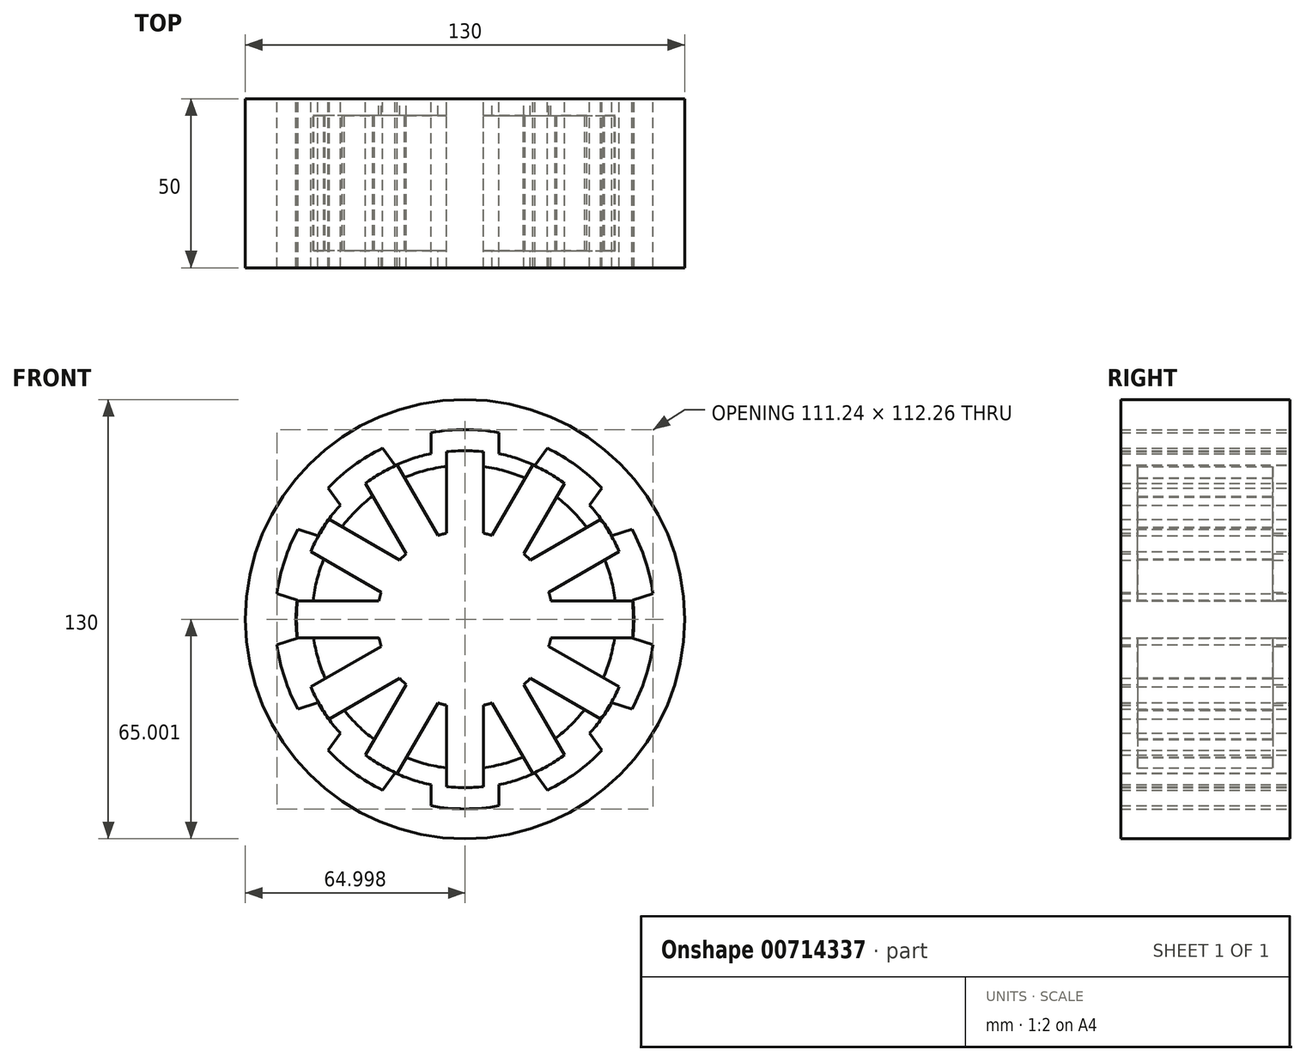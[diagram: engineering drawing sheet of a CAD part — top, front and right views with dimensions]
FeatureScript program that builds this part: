
annotation { "Feature Type Name" : "Feature", "Feature Type Description" : "" }
export const myFeature = defineFeature(function(context is Context, id is Id, definition is map)
    precondition{}
    {
        {
            var Q0;
            Q0=qCreatedBy(makeId("Front.planeOp"),FACE);
            var sketch = newSketch(context, id + "F0", { "sketchPlane" : qUnion([Q0])});
            skLineSegment(sketch, "E0.left", {"start": v(-130.96, 40.1) * mm, "end": v(-130.96, 33.86) * mm});
            skLineSegment(sketch, "E0.right", {"start": v(-110.96, 40.1) * mm, "end": v(-110.96, 33.86) * mm});
            skLineSegment(sketch, "E1.1.0", {"start": v(-145.34, 35.43) * mm, "end": v(-141.67, 30.38) * mm});
            skLineSegment(sketch, "E1.1.3", {"start": v(-161.52, 23.68) * mm, "end": v(-157.85, 18.63) * mm});
            skLineSegment(sketch, "E1.2.0", {"start": v(-170.4, 11.45) * mm, "end": v(-164.46, 9.52) * mm});
            skLineSegment(sketch, "E1.2.3", {"start": v(-176.58, -7.57) * mm, "end": v(-170.64, -9.5) * mm});
            skLineSegment(sketch, "E1.3.0", {"start": v(-176.58, -22.69) * mm, "end": v(-170.64, -20.76) * mm});
            skLineSegment(sketch, "E1.3.3", {"start": v(-170.4, -41.7) * mm, "end": v(-164.46, -39.78) * mm});
            skLineSegment(sketch, "E1.4.0", {"start": v(-161.52, -53.94) * mm, "end": v(-157.85, -48.89) * mm});
            skLineSegment(sketch, "E1.4.3", {"start": v(-145.34, -65.7) * mm, "end": v(-141.67, -60.64) * mm});
            skLineSegment(sketch, "E1.5.0", {"start": v(-130.96, -70.36) * mm, "end": v(-130.96, -64.12) * mm});
            skLineSegment(sketch, "E1.5.3", {"start": v(-110.96, -70.36) * mm, "end": v(-110.96, -64.12) * mm});
            skLineSegment(sketch, "E1.6.0", {"start": v(-96.59, -65.7) * mm, "end": v(-100.26, -60.64) * mm});
            skLineSegment(sketch, "E1.6.3", {"start": v(-80.4, -53.94) * mm, "end": v(-84.08, -48.89) * mm});
            skLineSegment(sketch, "E1.7.0", {"start": v(-71.52, -41.7) * mm, "end": v(-77.46, -39.78) * mm});
            skLineSegment(sketch, "E1.7.3", {"start": v(-65.34, -22.69) * mm, "end": v(-71.28, -20.76) * mm});
            skLineSegment(sketch, "E1.8.0", {"start": v(-65.34, -7.57) * mm, "end": v(-71.28, -9.5) * mm});
            skLineSegment(sketch, "E1.8.3", {"start": v(-71.52, 11.45) * mm, "end": v(-77.46, 9.52) * mm});
            skLineSegment(sketch, "E1.9.0", {"start": v(-80.4, 23.68) * mm, "end": v(-84.08, 18.63) * mm});
            skLineSegment(sketch, "E1.9.3", {"start": v(-96.59, 35.43) * mm, "end": v(-100.26, 30.38) * mm});
            skArc(sketch, "E2", {"start": v(-130.96, 33.86) * mm, "mid": v(-136.41, 32.42) * mm, "end": v(-141.67, 30.38) * mm});
            skCircle(sketch, "E3", {"center": v(-120.96, -15.13) * mm, "radius": 65 * mm});
            skArc(sketch, "E4", {"start": v(-145.34, 35.43) * mm, "mid": v(-153.95, 30.28) * mm, "end": v(-161.52, 23.68) * mm});
            skArc(sketch, "E5.trimOffspring", {"start": v(-157.85, 18.63) * mm, "mid": v(-161.41, 14.26) * mm, "end": v(-164.46, 9.52) * mm});
            skArc(sketch, "E6.trimOffspring", {"start": v(-170.64, -9.5) * mm, "mid": v(-170.96, -15.13) * mm, "end": v(-170.64, -20.76) * mm});
            skArc(sketch, "E7.trimOffspring", {"start": v(-164.46, -39.78) * mm, "mid": v(-161.41, -44.52) * mm, "end": v(-157.85, -48.89) * mm});
            skArc(sketch, "E8.trimOffspring", {"start": v(-141.67, -60.64) * mm, "mid": v(-136.41, -62.68) * mm, "end": v(-130.96, -64.12) * mm});
            skArc(sketch, "E9.trimOffspring", {"start": v(-110.96, -64.12) * mm, "mid": v(-105.51, -62.68) * mm, "end": v(-100.26, -60.64) * mm});
            skArc(sketch, "E10.trimOffspring", {"start": v(-84.08, -48.89) * mm, "mid": v(-80.51, -44.52) * mm, "end": v(-77.46, -39.78) * mm});
            skArc(sketch, "E11.trimOffspring", {"start": v(-71.28, -20.76) * mm, "mid": v(-70.96, -15.13) * mm, "end": v(-71.28, -9.5) * mm});
            skArc(sketch, "E12.trimOffspring", {"start": v(-77.46, 9.52) * mm, "mid": v(-80.51, 14.26) * mm, "end": v(-84.08, 18.63) * mm});
            skArc(sketch, "E13.trimOffspring", {"start": v(-100.26, 30.38) * mm, "mid": v(-105.51, 32.42) * mm, "end": v(-110.96, 33.86) * mm});
            skArc(sketch, "E14.trimOffspring", {"start": v(-110.96, 40.1) * mm, "mid": v(-120.96, 41) * mm, "end": v(-130.96, 40.1) * mm});
            skArc(sketch, "E15.trimOffspring", {"start": v(-80.4, 23.68) * mm, "mid": v(-87.97, 30.28) * mm, "end": v(-96.59, 35.43) * mm});
            skArc(sketch, "E16.trimOffspring", {"start": v(-65.34, -7.57) * mm, "mid": v(-67.58, 2.22) * mm, "end": v(-71.52, 11.45) * mm});
            skArc(sketch, "E17.trimOffspring", {"start": v(-71.52, -41.7) * mm, "mid": v(-67.58, -32.47) * mm, "end": v(-65.34, -22.69) * mm});
            skArc(sketch, "E18.trimOffspring", {"start": v(-96.59, -65.7) * mm, "mid": v(-87.97, -60.54) * mm, "end": v(-80.4, -53.94) * mm});
            skArc(sketch, "E19.trimOffspring", {"start": v(-130.96, -70.36) * mm, "mid": v(-120.96, -71.26) * mm, "end": v(-110.96, -70.36) * mm});
            skArc(sketch, "E20.trimOffspring", {"start": v(-161.52, -53.94) * mm, "mid": v(-153.95, -60.54) * mm, "end": v(-145.34, -65.7) * mm});
            skArc(sketch, "E21.trimOffspring", {"start": v(-176.58, -22.69) * mm, "mid": v(-174.35, -32.47) * mm, "end": v(-170.4, -41.7) * mm});
            skArc(sketch, "E22.trimOffspring", {"start": v(-170.4, 11.45) * mm, "mid": v(-174.35, 2.22) * mm, "end": v(-176.58, -7.57) * mm});
            skPoint(sketch, "E23.firstSnap0", {"position": v(-136.41, 32.42) * mm});
            skLineSegment(sketch, "E23.right", {"start": v(-126.42, 32.42) * mm, "end": v(-126.42, 10.28) * mm});
            skLineSegment(sketch, "E24.MirrorCS", {"start": v(-120.96, 32.42) * mm, "end": v(-115.5, 32.42) * mm});
            skLineSegment(sketch, "E25.MirrorCS", {"start": v(-115.5, 32.42) * mm, "end": v(-115.5, 10.28) * mm});
            skPoint(sketch, "E23.bottom.start.orphan", {"position": v(-120.96, 32.42) * mm});
            skArc(sketch, "E26", {"start": v(-115.5, 34.41) * mm, "mid": v(-120.96, 34.71) * mm, "end": v(-126.42, 34.41) * mm});
            skPoint(sketch, "E27.orphan", {"position": v(-115.5, 43.84) * mm});
            skArc(sketch, "E28.1.3", {"start": v(-141, 30.5) * mm, "mid": v(-145.88, 28.04) * mm, "end": v(-150.46, 25.05) * mm});
            skArc(sketch, "E28.2.3", {"start": v(-161.14, 14.37) * mm, "mid": v(-164.13, 9.8) * mm, "end": v(-166.6, 4.92) * mm});
            skArc(sketch, "E29.9.3.0", {"start": v(-170.5, -9.68) * mm, "mid": v(-170.8, -15.13) * mm, "end": v(-170.5, -20.58) * mm});
            skArc(sketch, "E29.9.4.0", {"start": v(-166.6, -35.18) * mm, "mid": v(-164.13, -40.05) * mm, "end": v(-161.14, -44.62) * mm});
            skArc(sketch, "E29.9.5.0", {"start": v(-150.46, -55.3) * mm, "mid": v(-145.88, -58.3) * mm, "end": v(-141, -60.76) * mm});
            skLineSegment(sketch, "E29.3.6.0", {"start": v(-126.42, -40.6) * mm, "end": v(-126.42, -64.67) * mm});
            skArc(sketch, "E29.9.6.0", {"start": v(-126.42, -64.67) * mm, "mid": v(-120.96, -64.97) * mm, "end": v(-115.5, -64.67) * mm});
            skLineSegment(sketch, "E29.1.7.0", {"start": v(-103.5, -34.45) * mm, "end": v(-91.47, -55.3) * mm});
            skArc(sketch, "E29.9.7.0", {"start": v(-100.91, -60.76) * mm, "mid": v(-96.04, -58.3) * mm, "end": v(-91.47, -55.3) * mm});
            skLineSegment(sketch, "E29.3.8.0", {"start": v(-101.64, -32.58) * mm, "end": v(-80.78, -44.62) * mm});
            skArc(sketch, "E29.9.8.0", {"start": v(-80.78, -44.62) * mm, "mid": v(-77.8, -40.05) * mm, "end": v(-75.33, -35.18) * mm});
            skLineSegment(sketch, "E29.3.9.0", {"start": v(-95.5, -20.58) * mm, "end": v(-71.42, -20.58) * mm});
            skArc(sketch, "E29.9.9.0", {"start": v(-71.42, -20.58) * mm, "mid": v(-71.12, -15.13) * mm, "end": v(-71.42, -9.68) * mm});
            skArc(sketch, "E29.9.10.0", {"start": v(-75.33, 4.92) * mm, "mid": v(-77.8, 9.8) * mm, "end": v(-80.78, 14.37) * mm});
            skArc(sketch, "E29.9.11.0", {"start": v(-91.47, 25.05) * mm, "mid": v(-96.04, 28.04) * mm, "end": v(-100.91, 30.5) * mm});
            skArc(sketch, "E30", {"start": v(-126.42, 10.33) * mm, "mid": v(-127.7, 10.02) * mm, "end": v(-128.97, 9.65) * mm});
            skLineSegment(sketch, "E31.trimOffspring", {"start": v(-146.43, -9.68) * mm, "end": v(-170.5, -9.68) * mm});
            skLineSegment(sketch, "E32.trimOffspring", {"start": v(-96.18, -23.14) * mm, "end": v(-75.33, -35.18) * mm});
            skLineSegment(sketch, "E33.trimOffspring", {"start": v(-103.5, 4.2) * mm, "end": v(-91.47, 25.05) * mm});
            skLineSegment(sketch, "E34.trimOffspring", {"start": v(-145.74, -7.12) * mm, "end": v(-166.6, 4.92) * mm});
            skLineSegment(sketch, "E35.trimOffspring", {"start": v(-138.42, 4.2) * mm, "end": v(-150.46, 25.05) * mm});
            skLineSegment(sketch, "E36.trimOffspring", {"start": v(-140.29, 2.33) * mm, "end": v(-161.14, 14.37) * mm});
            skLineSegment(sketch, "E37.trimOffspring", {"start": v(-128.97, 9.65) * mm, "end": v(-141, 30.5) * mm});
            skLineSegment(sketch, "E38.trimOffspring", {"start": v(-126.42, 10.28) * mm, "end": v(-126.42, 34.41) * mm});
            skLineSegment(sketch, "E39.trimOffspring", {"start": v(-115.5, 10.28) * mm, "end": v(-115.5, 34.41) * mm});
            skLineSegment(sketch, "E40.trimOffspring", {"start": v(-112.95, 9.65) * mm, "end": v(-100.91, 30.5) * mm});
            skArc(sketch, "E41.trimOffspring", {"start": v(-138.42, 4.2) * mm, "mid": v(-139.38, 3.28) * mm, "end": v(-140.29, 2.33) * mm});
            skArc(sketch, "E42.trimOffspring", {"start": v(-145.74, -7.12) * mm, "mid": v(-146.12, -8.39) * mm, "end": v(-146.43, -9.68) * mm});
            skArc(sketch, "E43.trimOffspring", {"start": v(-146.43, -20.58) * mm, "mid": v(-146.12, -21.87) * mm, "end": v(-145.74, -23.14) * mm});
            skLineSegment(sketch, "E44.trimOffspring", {"start": v(-146.43, -20.58) * mm, "end": v(-170.5, -20.58) * mm});
            skLineSegment(sketch, "E45.trimOffspring", {"start": v(-145.74, -23.14) * mm, "end": v(-166.6, -35.18) * mm});
            skLineSegment(sketch, "E46.trimOffspring", {"start": v(-140.29, -32.58) * mm, "end": v(-161.14, -44.62) * mm});
            skLineSegment(sketch, "E47.trimOffspring", {"start": v(-138.42, -34.45) * mm, "end": v(-150.46, -55.3) * mm});
            skArc(sketch, "E48.trimOffspring", {"start": v(-140.29, -32.58) * mm, "mid": v(-139.38, -33.54) * mm, "end": v(-138.42, -34.45) * mm});
            skLineSegment(sketch, "E49.trimOffspring", {"start": v(-128.97, -39.9) * mm, "end": v(-141, -60.76) * mm});
            skLineSegment(sketch, "E50.trimOffspring", {"start": v(-112.95, -39.9) * mm, "end": v(-100.91, -60.76) * mm});
            skLineSegment(sketch, "E51.trimOffspring", {"start": v(-115.5, -40.6) * mm, "end": v(-115.5, -64.67) * mm});
            skLineSegment(sketch, "E52.trimOffspring", {"start": v(-95.5, -9.68) * mm, "end": v(-71.42, -9.68) * mm});
            skLineSegment(sketch, "E53.trimOffspring", {"start": v(-96.18, -7.12) * mm, "end": v(-75.33, 4.92) * mm});
            skLineSegment(sketch, "E54.trimOffspring", {"start": v(-101.64, 2.33) * mm, "end": v(-80.78, 14.37) * mm});
            skArc(sketch, "E55.trimOffspring", {"start": v(-112.95, 9.65) * mm, "mid": v(-114.22, 10.02) * mm, "end": v(-115.5, 10.33) * mm});
            skArc(sketch, "E56.trimOffspring", {"start": v(-101.64, 2.33) * mm, "mid": v(-102.55, 3.28) * mm, "end": v(-103.5, 4.2) * mm});
            skArc(sketch, "E57.trimOffspring", {"start": v(-95.5, -9.68) * mm, "mid": v(-95.8, -8.39) * mm, "end": v(-96.18, -7.12) * mm});
            skArc(sketch, "E58.trimOffspring", {"start": v(-96.18, -23.14) * mm, "mid": v(-95.8, -21.87) * mm, "end": v(-95.5, -20.58) * mm});
            skArc(sketch, "E59.trimOffspring", {"start": v(-103.5, -34.45) * mm, "mid": v(-102.55, -33.54) * mm, "end": v(-101.64, -32.58) * mm});
            skArc(sketch, "E60.trimOffspring", {"start": v(-115.5, -40.6) * mm, "mid": v(-114.22, -40.28) * mm, "end": v(-112.95, -39.9) * mm});
            skArc(sketch, "E61.trimOffspring", {"start": v(-128.97, -39.9) * mm, "mid": v(-127.7, -40.28) * mm, "end": v(-126.42, -40.6) * mm});
            skSolve(sketch);
        }
        {
            var Q0;
            Q0=qCreatedBy(makeId("Front.planeOp"),FACE);
            var sketch = newSketch(context, id + "F1", { "sketchPlane" : qUnion([Q0])});
            skCircle(sketch, "E62", {"center": v(-121.22, -14.53) * mm, "radius": 44.92 * mm});
            skSolve(sketch);
        }
        {
            var Q0;
            Q0=makeQuery(id+"F0.imprint","IMPRINT",FACE,{"disambiguationData":[TD([[makeQuery(id+"F0.imprint","IMPRINT",EDGE,{"derivedFrom":sQuery(id+"F0.wireOp",EDGE,"E0.left")}),-1.0]])]});
            extrude(context, id + "F2", {"entities" : qUnion([Q0]), "endBound" : BoundingType.SYMMETRIC, "depth" : 50 * mm, "offsetDistance" : 25 * mm});
        }
        {
            var Q0;
            {var subQ3=sQuery(id+"F0.wireOp",EDGE,"E26");Q0=makeQuery(id+"F0.imprint","IMPRINT",FACE,{"disambiguationData":[TD([[makeQuery(id+"F0.imprint","IMPRINT",EDGE,{"derivedFrom":subQ3}),1.0]])]});}
            extrude(context, id + "F3", {"entities" : qUnion([Q0]), "endBound" : BoundingType.SYMMETRIC, "depth" : 50 * mm, "offsetDistance" : 25 * mm});
        }
        {
            var Q0;
            Q0 = qSketchRegion(id + "F1", true);
            extrude(context, id + "F4", {"entities" : qUnion([Q0]), "operationType" : NewBodyOperationType.ADD, "endBound" : BoundingType.SYMMETRIC, "depth" : 40 * mm, "offsetDistance" : 25 * mm});
        }
    });
